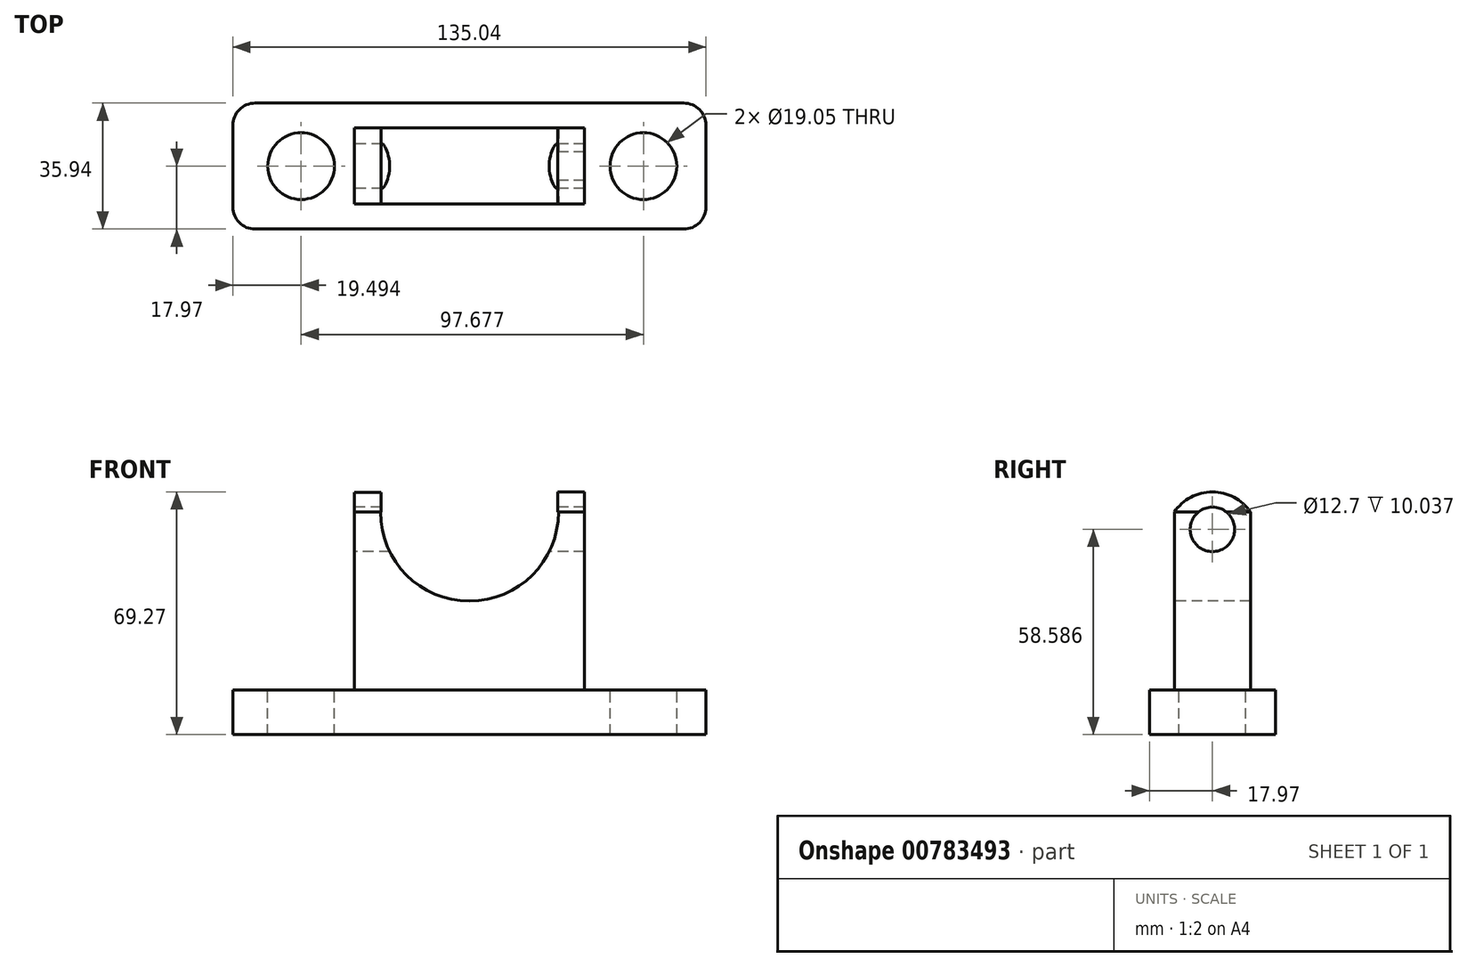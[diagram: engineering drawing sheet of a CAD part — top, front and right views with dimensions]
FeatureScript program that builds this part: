
annotation { "Feature Type Name" : "Feature", "Feature Type Description" : "" }
export const myFeature = defineFeature(function(context is Context, id is Id, definition is map)
    precondition{}
    {
        {
            var Q0;
            Q0=qCreatedBy(makeId("Top.planeOp"),FACE);
            var sketch = newSketch(context, id + "F0", { "sketchPlane" : qUnion([Q0])});
            skLineSegment(sketch, "E0.bottom", {"start": v(61.17, 17.97) * mm, "end": v(-61.17, 17.97) * mm});
            skLineSegment(sketch, "E0.top", {"start": v(61.17, -17.97) * mm, "end": v(-61.17, -17.97) * mm});
            skLineSegment(sketch, "E0.left", {"start": v(67.52, 11.62) * mm, "end": v(67.52, -11.62) * mm});
            skLineSegment(sketch, "E0.right", {"start": v(-67.52, 11.62) * mm, "end": v(-67.52, -11.62) * mm});
            skPoint(sketch, "E0.middle", {"position": v(0, 0) * mm});
            skPoint(sketch, "E1.visualSharp", {"position": v(-67.52, 17.97) * mm});
            skArc(sketch, "E1.filletArc", {"start": v(-61.17, 17.97) * mm, "mid": v(-65.66, 16.11) * mm, "end": v(-67.52, 11.62) * mm});
            skPoint(sketch, "E2.visualSharp", {"position": v(67.52, 17.97) * mm});
            skArc(sketch, "E2.filletArc", {"start": v(67.52, 11.62) * mm, "mid": v(65.66, 16.11) * mm, "end": v(61.17, 17.97) * mm});
            skPoint(sketch, "E3.visualSharp", {"position": v(67.52, -17.97) * mm});
            skArc(sketch, "E3.filletArc", {"start": v(61.17, -17.97) * mm, "mid": v(65.66, -16.11) * mm, "end": v(67.52, -11.62) * mm});
            skPoint(sketch, "E4.visualSharp", {"position": v(-67.52, -17.97) * mm});
            skArc(sketch, "E4.filletArc", {"start": v(-67.52, -11.62) * mm, "mid": v(-65.66, -16.11) * mm, "end": v(-61.17, -17.97) * mm});
            skSolve(sketch);
        }
        {
            var Q0;
            Q0=makeQuery(id+"F0.imprint","IMPRINT",FACE,{"disambiguationData":[TD([[makeQuery(id+"F0.imprint","IMPRINT",EDGE,{"derivedFrom":sQuery(id+"F0.wireOp",EDGE,"E0.bottom")}),1.0]])]});
            extrude(context, id + "F1", {"entities" : qUnion([Q0]), "depth" : 12.7 * mm, "offsetDistance" : 25.4 * mm});
        }
        {
            var Q0;
            Q0=makeQuery(id+"F1.opExtrude","CAP_FACE",FACE,{"disambiguationData":[OSD([sQuery(id+"F0.wireOp",EDGE,"E0.bottom"),sQuery(id+"F0.wireOp",EDGE,"E0.top"),sQuery(id+"F0.wireOp",EDGE,"E0.left"),sQuery(id+"F0.wireOp",EDGE,"E0.right"),sQuery(id+"F0.wireOp",EDGE,"E1.filletArc"),sQuery(id+"F0.wireOp",EDGE,"E2.filletArc"),sQuery(id+"F0.wireOp",EDGE,"E3.filletArc"),sQuery(id+"F0.wireOp",EDGE,"E4.filletArc")])],"isStart":false});
            var sketch = newSketch(context, id + "F2", { "sketchPlane" : qUnion([Q0])});
            skLineSegment(sketch, "E5.bottom", {"start": v(32.8, 10.86) * mm, "end": v(-32.8, 10.86) * mm});
            skLineSegment(sketch, "E5.top", {"start": v(32.8, -10.86) * mm, "end": v(-32.8, -10.86) * mm});
            skLineSegment(sketch, "E5.left", {"start": v(32.8, 10.86) * mm, "end": v(32.8, -10.86) * mm});
            skLineSegment(sketch, "E5.right", {"start": v(-32.8, 10.86) * mm, "end": v(-32.8, -10.86) * mm});
            skPoint(sketch, "E5.middle", {"position": v(0, 0) * mm});
            skSolve(sketch);
        }
        {
            var Q0;
            Q0=makeQuery(id+"F2.imprint","IMPRINT",FACE,{"disambiguationData":[TD([[makeQuery(id+"F2.imprint","IMPRINT",EDGE,{"derivedFrom":sQuery(id+"F2.wireOp",EDGE,"E5.bottom")}),1.0]])]});
            extrude(context, id + "F3", {"entities" : qUnion([Q0]), "operationType" : NewBodyOperationType.ADD, "depth" : 50.8 * mm, "offsetDistance" : 25.4 * mm});
        }
        {
            var Q0;
            Q0=makeQuery(id+"F3.opExtrude","SWEPT_FACE",FACE,{"disambiguationData":[OSD([sQuery(id+"F2.wireOp",EDGE,"E5.top")])]});
            var sketch = newSketch(context, id + "F4", { "sketchPlane" : qUnion([Q0])});
            skPoint(sketch, "E6", {"position": v(0, 63.5) * mm});
            skSolve(sketch);
        }
        {
            var Q0;
            Q0=sQuery(id+"F4.wireOp",VERTEX,"E6");
            var Q1;
            Q1=makeQuery(id+"F1.opExtrude","SWEPT_BODY",BODY,{"disambiguationData":[OSD([sQuery(id+"F0.wireOp",EDGE,"E0.bottom"),sQuery(id+"F0.wireOp",EDGE,"E0.top"),sQuery(id+"F0.wireOp",EDGE,"E0.left"),sQuery(id+"F0.wireOp",EDGE,"E0.right"),sQuery(id+"F0.wireOp",EDGE,"E1.filletArc"),sQuery(id+"F0.wireOp",EDGE,"E2.filletArc"),sQuery(id+"F0.wireOp",EDGE,"E3.filletArc"),sQuery(id+"F0.wireOp",EDGE,"E4.filletArc")])]});
            hole(context, id + "F5", {"style" : HoleStyle.SIMPLE, "endStyle" : HoleEndStyle.THROUGH, "holeDiameter" : 50.8 * mm, "majorDiameter" : 6.35 * mm, "isTappedThrough" : true, "tappedDepth" : 12.7 * mm, "tapClearance" : 3, "locations" : qUnion([Q0]), "scope" : qUnion([Q1])});
        }
        {
            var Q0;
            Q0=makeQuery(id+"F3.opExtrude","SWEPT_FACE",FACE,{"disambiguationData":[OSD([sQuery(id+"F2.wireOp",EDGE,"E5.right")])]});
            var sketch = newSketch(context, id + "F6", { "sketchPlane" : qUnion([Q0])});
            skArc(sketch, "E7", {"start": v(10.86, 63.5) * mm, "mid": v(0, 69.11) * mm, "end": v(-10.86, 63.5) * mm});
            skSolve(sketch);
        }
        {
            var Q0;
            Q0=makeQuery(id+"F6.imprint","IMPRINT",FACE,{"disambiguationData":[TD([[makeQuery(id+"F6.imprint","IMPRINT",EDGE,{"derivedFrom":sQuery(id+"F6.wireOp",EDGE,"E7")}),1.0]])]});
            extrude(context, id + "F7", {"entities" : qUnion([Q0]), "operationType" : NewBodyOperationType.ADD, "oppositeDirection" : true, "depth" : 7.62 * mm, "offsetDistance" : 25.4 * mm});
        }
        {
            var Q0;
            Q0=makeQuery(id+"F3.opExtrude","SWEPT_FACE",FACE,{"disambiguationData":[OSD([sQuery(id+"F2.wireOp",EDGE,"E5.left")])]});
            var sketch = newSketch(context, id + "F8", { "sketchPlane" : qUnion([Q0])});
            skArc(sketch, "E8", {"start": v(10.86, 63.5) * mm, "mid": v(0, 69.27) * mm, "end": v(-10.86, 63.5) * mm});
            skSolve(sketch);
        }
        {
            var Q0;
            Q0=makeQuery(id+"F8.imprint","IMPRINT",FACE,{"disambiguationData":[TD([[makeQuery(id+"F8.imprint","IMPRINT",EDGE,{"derivedFrom":sQuery(id+"F8.wireOp",EDGE,"E8")}),1.0]])]});
            extrude(context, id + "F9", {"entities" : qUnion([Q0]), "oppositeDirection" : true, "depth" : 7.62 * mm, "offsetDistance" : 25.4 * mm});
        }
        {
            var Q0;
            Q0=makeQuery(id+"F1.opExtrude","CAP_FACE",FACE,{"disambiguationData":[OSD([sQuery(id+"F0.wireOp",EDGE,"E0.bottom"),sQuery(id+"F0.wireOp",EDGE,"E0.top"),sQuery(id+"F0.wireOp",EDGE,"E0.left"),sQuery(id+"F0.wireOp",EDGE,"E0.right"),sQuery(id+"F0.wireOp",EDGE,"E1.filletArc"),sQuery(id+"F0.wireOp",EDGE,"E2.filletArc"),sQuery(id+"F0.wireOp",EDGE,"E3.filletArc"),sQuery(id+"F0.wireOp",EDGE,"E4.filletArc")])],"isStart":false});
            var sketch = newSketch(context, id + "F10", { "sketchPlane" : qUnion([Q0])});
            skPoint(sketch, "E9", {"position": v(-48.03, 0) * mm});
            skPoint(sketch, "E9.positionSnap0", {"position": v(-67.52, 0) * mm});
            skPoint(sketch, "E10", {"position": v(67.52, 0) * mm});
            skPoint(sketch, "E11", {"position": v(52.5, 0) * mm});
            skSolve(sketch);
        }
        {
            var Q0;
            Q0=sQuery(id+"F10.wireOp",VERTEX,"E9");
            var Q1;
            Q1=makeQuery(id+"F1.opExtrude","SWEPT_BODY",BODY,{"disambiguationData":[OSD([sQuery(id+"F0.wireOp",EDGE,"E0.bottom"),sQuery(id+"F0.wireOp",EDGE,"E0.top"),sQuery(id+"F0.wireOp",EDGE,"E0.left"),sQuery(id+"F0.wireOp",EDGE,"E0.right"),sQuery(id+"F0.wireOp",EDGE,"E1.filletArc"),sQuery(id+"F0.wireOp",EDGE,"E2.filletArc"),sQuery(id+"F0.wireOp",EDGE,"E3.filletArc"),sQuery(id+"F0.wireOp",EDGE,"E4.filletArc")])]});
            hole(context, id + "F11", {"style" : HoleStyle.SIMPLE, "endStyle" : HoleEndStyle.THROUGH, "holeDiameter" : 19.05 * mm, "majorDiameter" : 6.35 * mm, "isTappedThrough" : true, "tappedDepth" : 12.7 * mm, "tapClearance" : 3, "locations" : qUnion([Q0]), "scope" : qUnion([Q1])});
        }
        {
            var Q0;
            Q0=makeQuery(id+"F1.opExtrude","CAP_FACE",FACE,{"disambiguationData":[OSD([sQuery(id+"F0.wireOp",EDGE,"E0.bottom"),sQuery(id+"F0.wireOp",EDGE,"E0.top"),sQuery(id+"F0.wireOp",EDGE,"E0.left"),sQuery(id+"F0.wireOp",EDGE,"E0.right"),sQuery(id+"F0.wireOp",EDGE,"E1.filletArc"),sQuery(id+"F0.wireOp",EDGE,"E2.filletArc"),sQuery(id+"F0.wireOp",EDGE,"E3.filletArc"),sQuery(id+"F0.wireOp",EDGE,"E4.filletArc")])],"isStart":false});
            var sketch = newSketch(context, id + "F12", { "sketchPlane" : qUnion([Q0])});
            skPoint(sketch, "E12", {"position": v(49.65, 0) * mm});
            skSolve(sketch);
        }
        {
            var Q0;
            Q0=sQuery(id+"F12.wireOp",VERTEX,"E12");
            var Q1;
            Q1=makeQuery(id+"F1.opExtrude","SWEPT_BODY",BODY,{"disambiguationData":[OSD([sQuery(id+"F0.wireOp",EDGE,"E0.bottom"),sQuery(id+"F0.wireOp",EDGE,"E0.top"),sQuery(id+"F0.wireOp",EDGE,"E0.left"),sQuery(id+"F0.wireOp",EDGE,"E0.right"),sQuery(id+"F0.wireOp",EDGE,"E1.filletArc"),sQuery(id+"F0.wireOp",EDGE,"E2.filletArc"),sQuery(id+"F0.wireOp",EDGE,"E3.filletArc"),sQuery(id+"F0.wireOp",EDGE,"E4.filletArc")])]});
            hole(context, id + "F13", {"style" : HoleStyle.SIMPLE, "endStyle" : HoleEndStyle.THROUGH, "holeDiameter" : 19.05 * mm, "majorDiameter" : 6.35 * mm, "isTappedThrough" : true, "tappedDepth" : 12.7 * mm, "tapClearance" : 3, "locations" : qUnion([Q0]), "scope" : qUnion([Q1])});
        }
        {
            var Q0;
            {var subQ0=sQuery(id+"F2.wireOp",EDGE,"E5.right");Q0=makeQuery(id+"F7.boolean.opBoolean","MERGE",FACE,{"derivedFrom":[makeQuery(id+"F3.opExtrude","SWEPT_FACE",FACE,{"disambiguationData":[OSD([subQ0])]}),makeQuery(id+"F7.opExtrude","CAP_FACE",FACE,{"disambiguationData":[OSD([subQ0,sQuery(id+"F6.wireOp",EDGE,"E7")])],"isStart":true})]});}
            var sketch = newSketch(context, id + "F14", { "sketchPlane" : qUnion([Q0])});
            skPoint(sketch, "E13", {"position": v(0, 58.59) * mm});
            skSolve(sketch);
        }
        {
            var Q0;
            Q0=sQuery(id+"F14.wireOp",VERTEX,"E13");
            var Q1;
            Q1=makeQuery(id+"F1.opExtrude","SWEPT_BODY",BODY,{"disambiguationData":[OSD([sQuery(id+"F0.wireOp",EDGE,"E0.bottom"),sQuery(id+"F0.wireOp",EDGE,"E0.top"),sQuery(id+"F0.wireOp",EDGE,"E0.left"),sQuery(id+"F0.wireOp",EDGE,"E0.right"),sQuery(id+"F0.wireOp",EDGE,"E1.filletArc"),sQuery(id+"F0.wireOp",EDGE,"E2.filletArc"),sQuery(id+"F0.wireOp",EDGE,"E3.filletArc"),sQuery(id+"F0.wireOp",EDGE,"E4.filletArc")])]});
            var Q2;
            Q2=makeQuery(id+"F9.opExtrude","SWEPT_BODY",BODY,{"disambiguationData":[OSD([sQuery(id+"F2.wireOp",EDGE,"E5.left"),sQuery(id+"F8.wireOp",EDGE,"E8")])]});
            hole(context, id + "F15", {"style" : HoleStyle.SIMPLE, "endStyle" : HoleEndStyle.THROUGH, "holeDiameter" : 12.7 * mm, "majorDiameter" : 6.35 * mm, "isTappedThrough" : true, "tappedDepth" : 12.7 * mm, "tapClearance" : 3, "locations" : qUnion([Q0]), "scope" : qUnion([Q1, Q2])});
        }
    });
